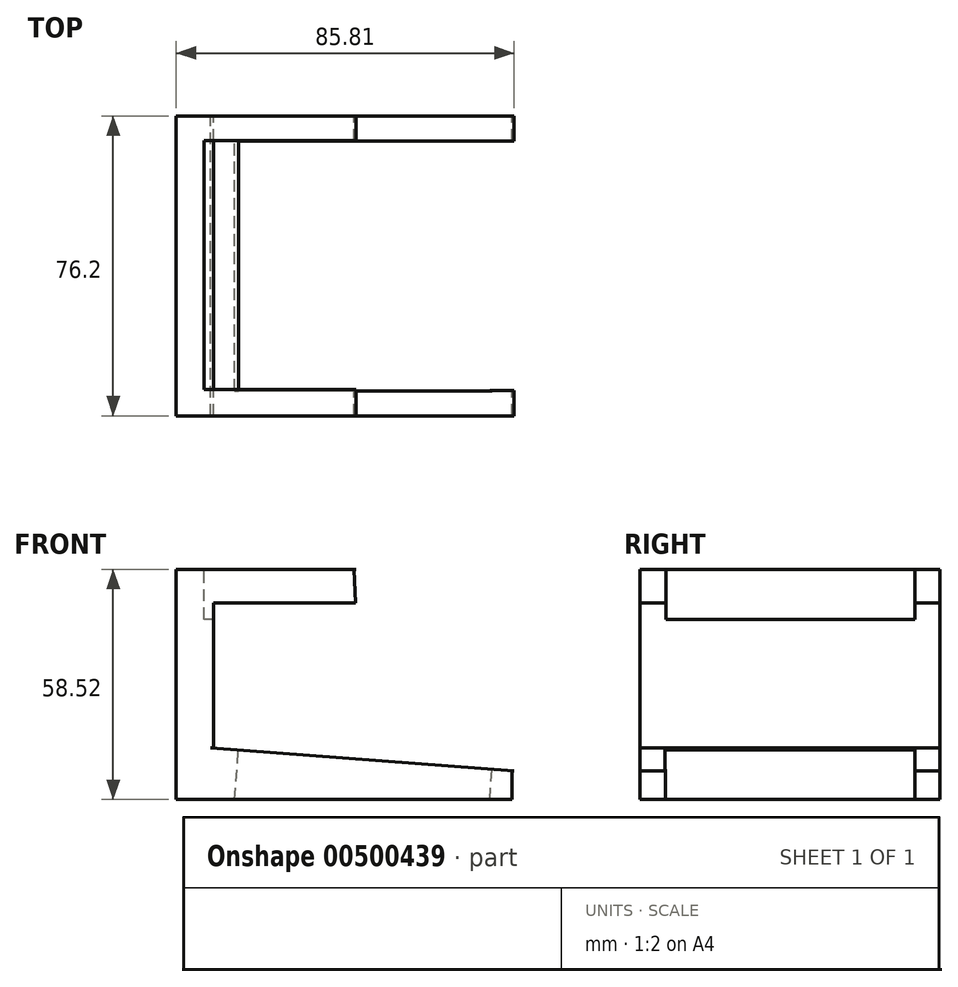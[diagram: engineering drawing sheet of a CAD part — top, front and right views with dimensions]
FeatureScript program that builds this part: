
annotation { "Feature Type Name" : "Feature", "Feature Type Description" : "" }
export const myFeature = defineFeature(function(context is Context, id is Id, definition is map)
    precondition{}
    {
        {
            var Q0;
            Q0=qCreatedBy(makeId("Front.planeOp"),FACE);
            var sketch = newSketch(context, id + "F0", { "sketchPlane" : qUnion([Q0])});
            skLineSegment(sketch, "E0", {"start": v(45.57, -24.08) * mm, "end": v(-41, -24.08) * mm});
            skLineSegment(sketch, "E1", {"start": v(45.57, -24.08) * mm, "end": v(45.57, -16.76) * mm});
            skLineSegment(sketch, "E2", {"start": v(45.57, -16.76) * mm, "end": v(-31.55, -10.97) * mm});
            skLineSegment(sketch, "E3", {"start": v(-41, -24.08) * mm, "end": v(-41, 34.44) * mm});
            skLineSegment(sketch, "E4", {"start": v(-31.55, -10.97) * mm, "end": v(-31.55, 25.9) * mm});
            skLineSegment(sketch, "E5", {"start": v(-31.55, 25.9) * mm, "end": v(5.03, 25.9) * mm});
            skLineSegment(sketch, "E6", {"start": v(-41, 34.44) * mm, "end": v(4.72, 34.44) * mm});
            skLineSegment(sketch, "E7", {"start": v(4.72, 34.44) * mm, "end": v(5.03, 25.9) * mm});
            skSolve(sketch);
        }
        {
            var Q0;
            Q0 = qSketchRegion(id + "F0", true);
            extrude(context, id + "F1", {"entities" : qUnion([Q0]), "depth" : 76.2 * mm, "offsetDistance" : 25.4 * mm});
        }
        {
            var Q0;
            Q0=makeQuery(id+"F1.opExtrude","SWEPT_FACE",FACE,{"disambiguationData":[OSD([sQuery(id+"F0.wireOp",EDGE,"E2")])]});
            var sketch = newSketch(context, id + "F2", { "sketchPlane" : qUnion([Q0])});
            skSolve(sketch);
        }
        {
            var Q0;
            {var subQ0=sQuery(id+"F0.wireOp",EDGE,"E2");Q0=makeQuery(id+"F2.imprint","IMPRINT",FACE,{"disambiguationData":[TD([[makeQuery(id+"F2.imprint","IMPRINT",EDGE,{"derivedFrom":makeQuery(id+"F1.opExtrude","CAP_EDGE",EDGE,{"disambiguationData":[OSD([subQ0])],"isStart":true})}),1.0]])]});}
            var sketch = newSketch(context, id + "F3", { "sketchPlane" : qUnion([Q0])});
            skLineSegment(sketch, "E8.0", {"start": v(40.35, -69.85) * mm, "end": v(40.35, -6.35) * mm});
            skLineSegment(sketch, "E8.1", {"start": v(-24.29, -69.85) * mm, "end": v(40.35, -69.85) * mm});
            skLineSegment(sketch, "E8.2", {"start": v(-24.29, -6.35) * mm, "end": v(-24.29, -69.85) * mm});
            skLineSegment(sketch, "E8.3", {"start": v(40.35, -6.35) * mm, "end": v(-24.29, -6.35) * mm});
            skSolve(sketch);
        }
        {
            var Q0;
            Q0=makeQuery(id+"F3.imprint","IMPRINT",FACE,{"disambiguationData":[TD([[makeQuery(id+"F3.imprint","IMPRINT",EDGE,{"derivedFrom":sQuery(id+"F3.wireOp",EDGE,"E8.0")}),1.0]])]});
            extrude(context, id + "F4", {"entities" : qUnion([Q0]), "operationType" : NewBodyOperationType.REMOVE, "oppositeDirection" : true, "depth" : 12.7 * mm, "offsetDistance" : 25.4 * mm});
        }
        {
            var Q0;
            {var subQ0=sQuery(id+"F0.wireOp",EDGE,"E2");Q0=makeQuery(id+"F2.imprint","IMPRINT",FACE,{"disambiguationData":[TD([[makeQuery(id+"F2.imprint","IMPRINT",EDGE,{"derivedFrom":makeQuery(id+"F1.opExtrude","CAP_EDGE",EDGE,{"disambiguationData":[OSD([subQ0])],"isStart":true})}),1.0]])]});}
            var sketch = newSketch(context, id + "F5", { "sketchPlane" : qUnion([Q0])});
            skLineSegment(sketch, "E9", {"start": v(40.3, -69.78) * mm, "end": v(46.62, -69.78) * mm});
            skLineSegment(sketch, "E10", {"start": v(40.33, -6.34) * mm, "end": v(46.64, -6.34) * mm});
            skLineSegment(sketch, "E11", {"start": v(46.64, -6.34) * mm, "end": v(46.62, -69.78) * mm});
            skLineSegment(sketch, "E12", {"start": v(40.3, -69.78) * mm, "end": v(40.33, -6.34) * mm});
            skSolve(sketch);
        }
        {
            var Q0;
            Q0=makeQuery(id+"F5.imprint","IMPRINT",FACE,{"disambiguationData":[TD([[makeQuery(id+"F5.imprint","IMPRINT",EDGE,{"derivedFrom":sQuery(id+"F5.wireOp",EDGE,"E9")}),1.0]])]});
            extrude(context, id + "F6", {"entities" : qUnion([Q0]), "operationType" : NewBodyOperationType.REMOVE, "oppositeDirection" : true, "depth" : 25.4 * mm, "offsetDistance" : 25.4 * mm});
        }
        {
            var Q0;
            Q0=makeQuery(id+"F1.opExtrude","SWEPT_FACE",FACE,{"disambiguationData":[OSD([sQuery(id+"F0.wireOp",EDGE,"E1")])]});
            extrude(context, id + "F7", {"entities" : qUnion([Q0]), "operationType" : NewBodyOperationType.REMOVE, "oppositeDirection" : true, "depth" : 0.25 * mm, "offsetDistance" : 25.4 * mm});
        }
        {
            var Q0;
            Q0=makeQuery(id+"F7.boolean.opBoolean","COPY",FACE,{"derivedFrom":makeQuery(id+"F7.opExtrude","CAP_FACE",FACE,{"disambiguationData":[OSD([sQuery(id+"F0.wireOp",EDGE,"E1")])],"isStart":false})});
            extrude(context, id + "F8", {"entities" : qUnion([Q0]), "operationType" : NewBodyOperationType.REMOVE, "oppositeDirection" : true, "depth" : 0.25 * mm, "offsetDistance" : 25.4 * mm});
        }
        {
            var Q0;
            Q0=makeQuery(id+"F8.boolean.opBoolean","COPY",FACE,{"derivedFrom":makeQuery(id+"F8.opExtrude","CAP_FACE",FACE,{"disambiguationData":[OSD([sQuery(id+"F0.wireOp",EDGE,"E1")])],"isStart":false})});
            var Q1;
            {var subQ0=sQuery(id+"F0.wireOp",EDGE,"E2");Q1=makeQuery(id+"F2.imprint","IMPRINT",FACE,{"disambiguationData":[TD([[makeQuery(id+"F2.imprint","IMPRINT",EDGE,{"derivedFrom":makeQuery(id+"F1.opExtrude","CAP_EDGE",EDGE,{"disambiguationData":[OSD([subQ0])],"isStart":true})}),1.0]])]});}
            extrude(context, id + "F9", {"entities" : qUnion([Q0, Q1]), "operationType" : NewBodyOperationType.REMOVE, "oppositeDirection" : true, "depth" : 0.76 * mm, "offsetDistance" : 25.4 * mm});
        }
        {
            var Q0;
            Q0=makeQuery(id+"F1.opExtrude","SWEPT_FACE",FACE,{"disambiguationData":[OSD([sQuery(id+"F0.wireOp",EDGE,"E6")])]});
            var sketch = newSketch(context, id + "F10", { "sketchPlane" : qUnion([Q0])});
            skLineSegment(sketch, "E13", {"start": v(10.3, -69.55) * mm, "end": v(-34, -69.55) * mm});
            skLineSegment(sketch, "E14", {"start": v(10.3, -6.33) * mm, "end": v(-34, -6.33) * mm});
            skLineSegment(sketch, "E15", {"start": v(10.3, -6.33) * mm, "end": v(10.3, -69.55) * mm});
            skLineSegment(sketch, "E16", {"start": v(-34, -6.33) * mm, "end": v(-34, -69.55) * mm});
            skSolve(sketch);
        }
        {
            var Q0;
            {var subQ0=sQuery(id+"F10.wireOp",EDGE,"E16");Q0=makeQuery(id+"F10.imprint","IMPRINT",FACE,{"disambiguationData":[TD([[makeQuery(id+"F10.imprint","IMPRINT",EDGE,{"derivedFrom":subQ0}),1.0]])]});}
            extrude(context, id + "F11", {"entities" : qUnion([Q0]), "operationType" : NewBodyOperationType.REMOVE, "oppositeDirection" : true, "depth" : 12.7 * mm, "offsetDistance" : 25.4 * mm});
        }
        {
            var Q0;
            Q0=makeQuery(id+"F1.opExtrude","SWEPT_FACE",FACE,{"disambiguationData":[OSD([sQuery(id+"F0.wireOp",EDGE,"E7")])]});
            extrude(context, id + "F12", {"entities" : qUnion([Q0]), "operationType" : NewBodyOperationType.REMOVE, "oppositeDirection" : true, "depth" : 0.5 * mm, "offsetDistance" : 25.4 * mm});
        }
    });
